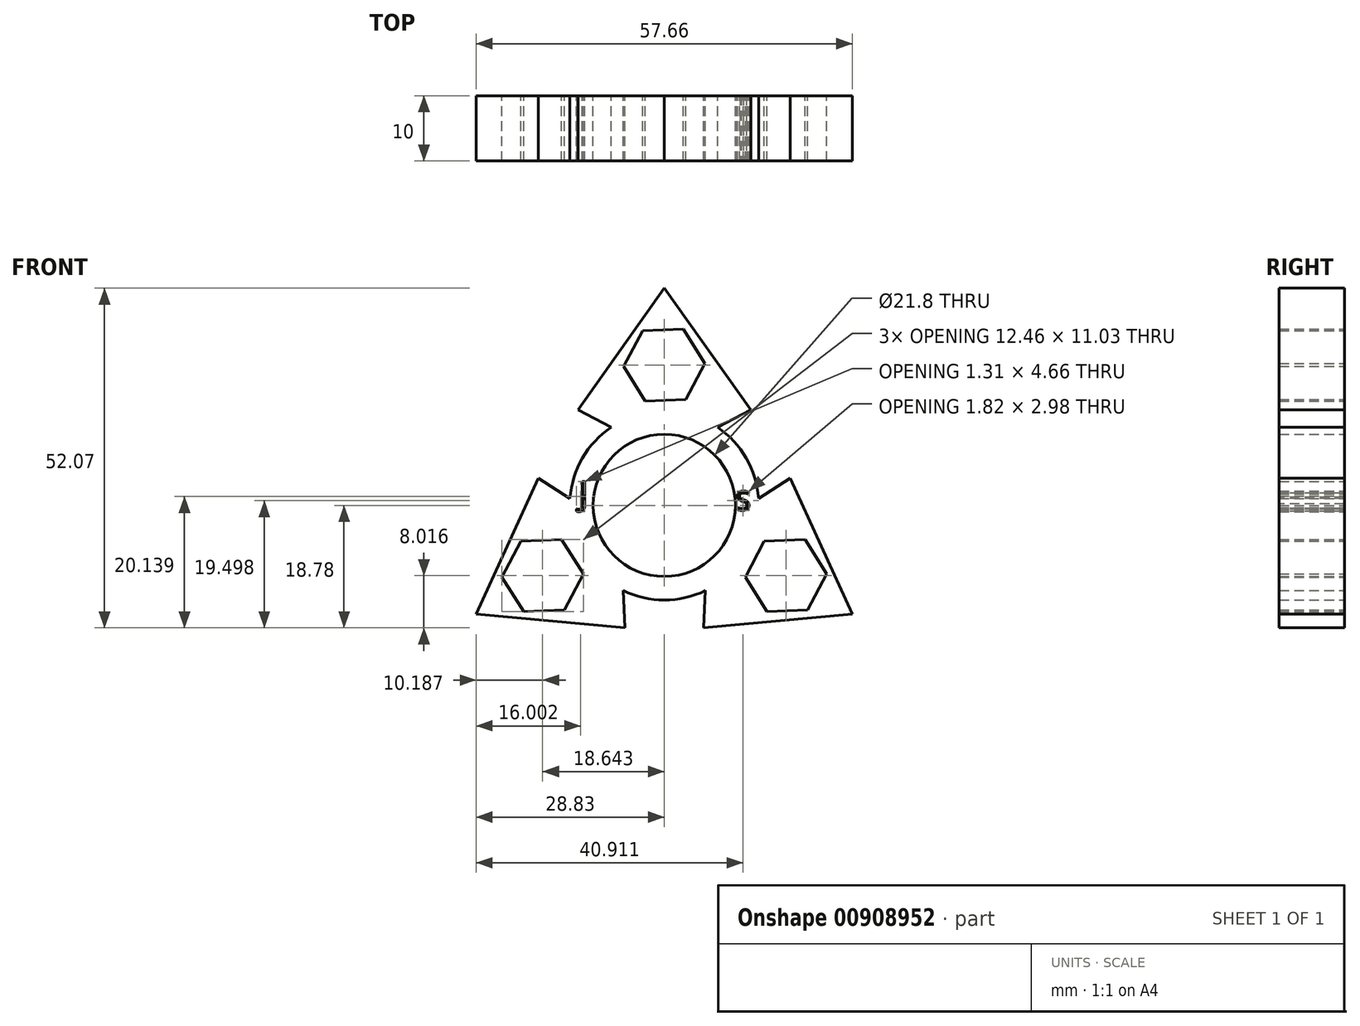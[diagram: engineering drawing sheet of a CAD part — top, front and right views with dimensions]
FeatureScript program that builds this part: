
annotation { "Feature Type Name" : "Feature", "Feature Type Description" : "" }
export const myFeature = defineFeature(function(context is Context, id is Id, definition is map)
    precondition{}
    {
        {
            var Q0;
            Q0=qCreatedBy(makeId("Front.planeOp"),FACE);
            var sketch = newSketch(context, id + "F0", { "sketchPlane" : qUnion([Q0])});
            skCircle(sketch, "E0", {"center": v(0, 0) * mm, "radius": 10.9 * mm});
            skArc(sketch, "E1", {"start": v(0.52, 14.5) * mm, "mid": v(0, 14.5) * mm, "end": v(-0.52, 14.5) * mm});
            skText(sketch, "E2", { "text": "J", "fontName": "OpenSans-Regular.ttf"});
            skText(sketch, "E3", { "text": "S\n", "fontName": "OpenSans-Regular.ttf"});
            skLineSegment(sketch, "E4.2.16", {"start": v(13.36, -12.5) * mm, "end": v(13.54, -12.6) * mm});
            skLineSegment(sketch, "E4.2.17", {"start": v(13.36, -12.5) * mm, "end": v(13.54, -12.6) * mm});
            skPoint(sketch, "E5", {"position": v(0, 21.53) * mm});
            skCircle(sketch, "E6.cCircle", {"center": v(0, 21.53) * mm, "radius": 5.4 * mm, "construction": true});
            skLineSegment(sketch, "E6.0", {"start": v(2.9, 27.04) * mm, "end": v(6.23, 21.77) * mm});
            skLineSegment(sketch, "E6.1", {"start": v(6.23, 21.77) * mm, "end": v(3.32, 16.25) * mm});
            skLineSegment(sketch, "E6.2", {"start": v(3.32, 16.25) * mm, "end": v(-2.9, 16.01) * mm});
            skLineSegment(sketch, "E6.3", {"start": v(-2.9, 16.01) * mm, "end": v(-6.23, 21.29) * mm});
            skLineSegment(sketch, "E6.4", {"start": v(-6.23, 21.29) * mm, "end": v(-3.32, 26.8) * mm});
            skLineSegment(sketch, "E6.5", {"start": v(-3.32, 26.8) * mm, "end": v(2.9, 27.04) * mm});
            skPoint(sketch, "E6.0.midPoint", {"position": v(4.57, 24.4) * mm});
            skLineSegment(sketch, "E7", {"start": v(0, 14.5) * mm, "end": v(0, 33.3) * mm});
            skLineSegment(sketch, "E8", {"start": v(0, 33.3) * mm, "end": v(13.23, 14.63) * mm});
            skLineSegment(sketch, "E9", {"start": v(13.23, 14.63) * mm, "end": v(7.17, 11.48) * mm});
            skLineSegment(sketch, "E10", {"start": v(7.17, 11.48) * mm, "end": v(0.2, 14.63) * mm});
            skPoint(sketch, "E10.endSnap0", {"position": v(0.2, 16.13) * mm});
            skLineSegment(sketch, "E11.MirrorCS", {"start": v(0, 33.3) * mm, "end": v(-13.23, 14.63) * mm});
            skLineSegment(sketch, "E12.MirrorCS", {"start": v(-13.23, 14.63) * mm, "end": v(-7.17, 11.48) * mm});
            skLineSegment(sketch, "E13.MirrorCS", {"start": v(-7.17, 11.48) * mm, "end": v(-0.2, 14.63) * mm});
            skPoint(sketch, "E14.1.0", {"position": v(-14.07, -7.89) * mm});
            skPoint(sketch, "E14.1.1", {"position": v(-18.64, -10.76) * mm});
            skLineSegment(sketch, "E14.1.2", {"start": v(-28.83, -16.65) * mm, "end": v(-19.29, 4.15) * mm});
            skLineSegment(sketch, "E14.1.3", {"start": v(-24.87, -11) * mm, "end": v(-21.96, -5.49) * mm});
            skPoint(sketch, "E14.1.4", {"position": v(-23.42, -8.24) * mm});
            skLineSegment(sketch, "E14.1.5", {"start": v(-6.05, -18.78) * mm, "end": v(-6.35, -11.95) * mm});
            skCircle(sketch, "E14.1.6", {"center": v(-18.64, -10.76) * mm, "radius": 5.4 * mm, "construction": true});
            skLineSegment(sketch, "E14.1.7", {"start": v(-15.32, -16.04) * mm, "end": v(-21.55, -16.28) * mm});
            skLineSegment(sketch, "E14.1.8", {"start": v(-28.83, -16.65) * mm, "end": v(-6.05, -18.78) * mm});
            skLineSegment(sketch, "E14.1.9", {"start": v(-12.41, -10.53) * mm, "end": v(-15.32, -16.04) * mm});
            skLineSegment(sketch, "E14.1.10", {"start": v(-21.96, -5.49) * mm, "end": v(-15.73, -5.25) * mm});
            skLineSegment(sketch, "E14.1.11", {"start": v(-6.35, -11.95) * mm, "end": v(-12.57, -7.5) * mm});
            skLineSegment(sketch, "E14.1.12", {"start": v(-13.53, 0.47) * mm, "end": v(-12.77, -7.14) * mm});
            skLineSegment(sketch, "E14.1.13", {"start": v(-12.56, -7.25) * mm, "end": v(-28.83, -16.65) * mm});
            skLineSegment(sketch, "E14.1.14", {"start": v(-15.73, -5.25) * mm, "end": v(-12.41, -10.53) * mm});
            skLineSegment(sketch, "E14.1.15", {"start": v(-19.29, 4.15) * mm, "end": v(-13.53, 0.47) * mm});
            skLineSegment(sketch, "E14.1.16", {"start": v(-21.55, -16.28) * mm, "end": v(-24.87, -11) * mm});
            skPoint(sketch, "E14.2.0", {"position": v(13.87, -8.24) * mm});
            skPoint(sketch, "E14.2.1", {"position": v(18.64, -10.76) * mm});
            skLineSegment(sketch, "E14.2.2", {"start": v(28.83, -16.65) * mm, "end": v(6.05, -18.78) * mm});
            skLineSegment(sketch, "E14.2.3", {"start": v(21.96, -16.04) * mm, "end": v(15.73, -16.28) * mm});
            skPoint(sketch, "E14.2.4", {"position": v(18.85, -16.16) * mm});
            skLineSegment(sketch, "E14.2.5", {"start": v(19.29, 4.15) * mm, "end": v(13.53, 0.47) * mm});
            skCircle(sketch, "E14.2.6", {"center": v(18.64, -10.76) * mm, "radius": 5.4 * mm, "construction": true});
            skLineSegment(sketch, "E14.2.7", {"start": v(21.55, -5.25) * mm, "end": v(24.87, -10.53) * mm});
            skLineSegment(sketch, "E14.2.8", {"start": v(28.83, -16.65) * mm, "end": v(19.29, 4.15) * mm});
            skLineSegment(sketch, "E14.2.9", {"start": v(15.32, -5.49) * mm, "end": v(21.55, -5.25) * mm});
            skLineSegment(sketch, "E14.2.10", {"start": v(15.73, -16.28) * mm, "end": v(12.41, -11) * mm});
            skLineSegment(sketch, "E14.2.11", {"start": v(13.53, 0.47) * mm, "end": v(12.77, -7.14) * mm});
            skLineSegment(sketch, "E14.2.12", {"start": v(6.35, -11.95) * mm, "end": v(12.57, -7.5) * mm});
            skLineSegment(sketch, "E14.2.13", {"start": v(12.56, -7.25) * mm, "end": v(28.83, -16.65) * mm});
            skLineSegment(sketch, "E14.2.14", {"start": v(12.41, -11) * mm, "end": v(15.32, -5.49) * mm});
            skLineSegment(sketch, "E14.2.15", {"start": v(6.05, -18.78) * mm, "end": v(6.35, -11.95) * mm});
            skLineSegment(sketch, "E14.2.16", {"start": v(24.87, -10.53) * mm, "end": v(21.96, -16.04) * mm});
            skArc(sketch, "E15.trimOffspring", {"start": v(-8.16, 11.99) * mm, "mid": v(-12.56, 7.25) * mm, "end": v(-14.46, 1.07) * mm});
            skArc(sketch, "E16.trimOffspring", {"start": v(14.46, 1.07) * mm, "mid": v(12.56, 7.25) * mm, "end": v(8.16, 11.99) * mm});
            skArc(sketch, "E17.trimOffspring", {"start": v(12.3, -7.7) * mm, "mid": v(12.56, -7.25) * mm, "end": v(12.8, -6.8) * mm});
            skArc(sketch, "E18.trimOffspring", {"start": v(-12.8, -6.8) * mm, "mid": v(-12.56, -7.25) * mm, "end": v(-12.3, -7.7) * mm});
            skArc(sketch, "E19.trimOffspring", {"start": v(-6.3, -13.06) * mm, "mid": v(0, -14.5) * mm, "end": v(6.3, -13.06) * mm});
            const initialGuessF0  = {"E2": [-0.01308, 0, 1, 0, 0.00372], "E3": [0.01096, -0.00073, 1, 0, 0.00292]};
            skSetInitialGuess(sketch, initialGuessF0);
            skSolve(sketch);
        }
        {
            var Q0;
            Q0 = qSketchRegion(id + "F0", true);
            extrude(context, id + "F1", {"entities" : qUnion([Q0]), "depth" : 10 * mm, "offsetDistance" : 25 * mm});
        }
    });
